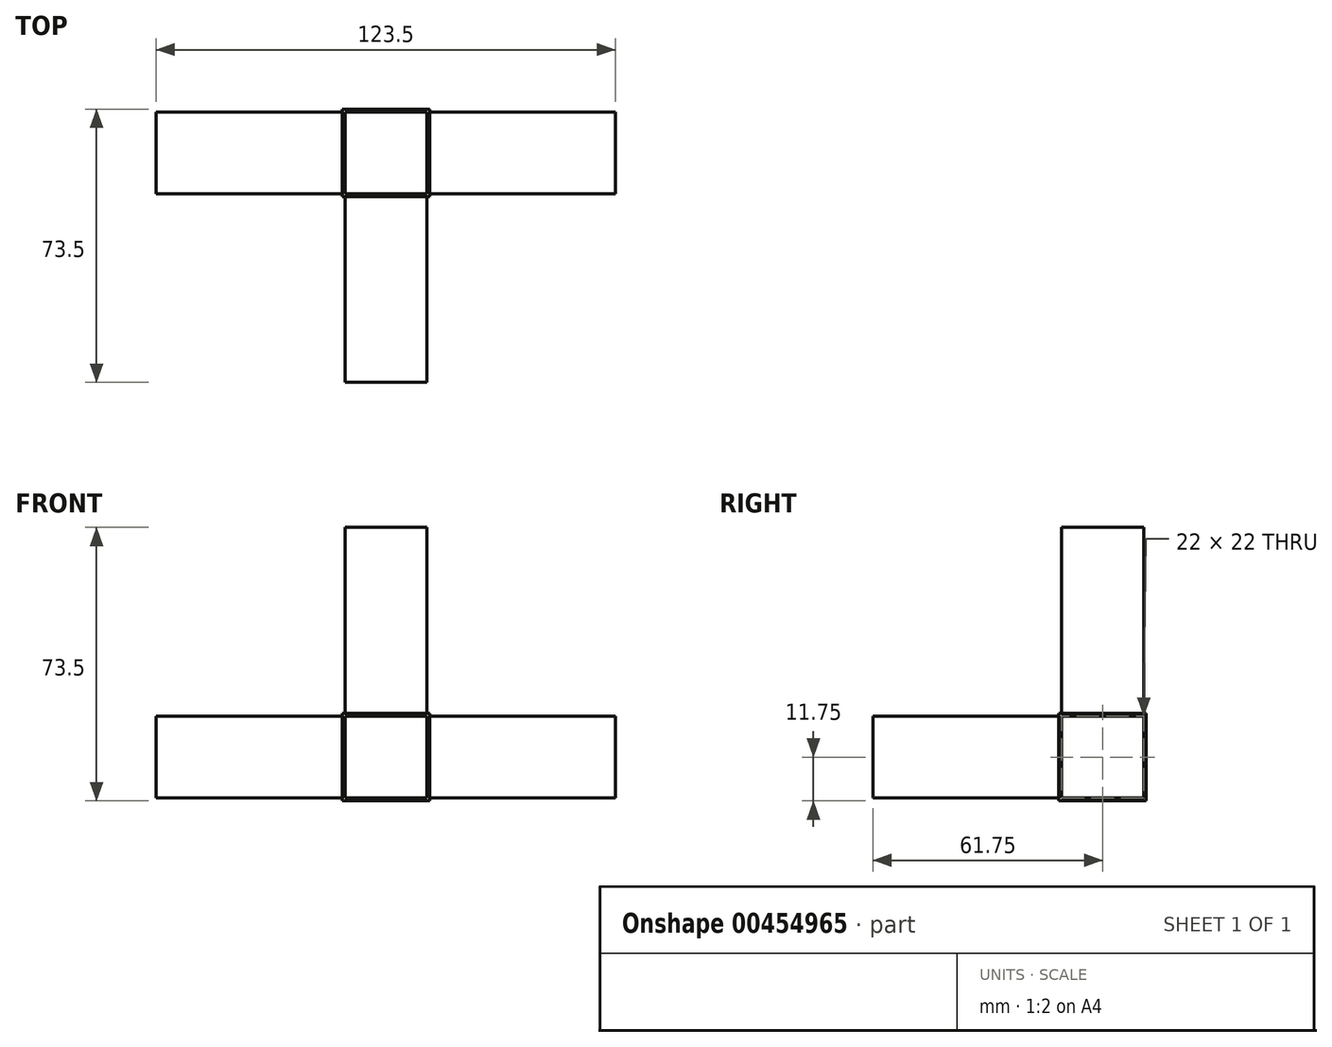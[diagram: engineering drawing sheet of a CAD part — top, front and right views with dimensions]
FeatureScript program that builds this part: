
annotation { "Feature Type Name" : "Feature", "Feature Type Description" : "" }
export const myFeature = defineFeature(function(context is Context, id is Id, definition is map)
    precondition{}
    {
        {
            var Q0;
            Q0=qCreatedBy(makeId("Front.planeOp"),FACE);
            var sketch = newSketch(context, id + "F0", { "sketchPlane" : qUnion([Q0])});
            skLineSegment(sketch, "E0.bottom", {"start": v(11.75, 11.75) * mm, "end": v(-11.75, 11.75) * mm});
            skLineSegment(sketch, "E0.top", {"start": v(11.75, -11.75) * mm, "end": v(-11.75, -11.75) * mm});
            skLineSegment(sketch, "E0.left", {"start": v(11.75, 11.75) * mm, "end": v(11.75, -11.75) * mm});
            skLineSegment(sketch, "E0.right", {"start": v(-11.75, 11.75) * mm, "end": v(-11.75, -11.75) * mm});
            skPoint(sketch, "E0.middle", {"position": v(0, 0) * mm});
            skSolve(sketch);
        }
        {
            var Q0;
            Q0 = qSketchRegion(id + "F0", true);
            extrude(context, id + "F1", {"entities" : qUnion([Q0]), "endBound" : BoundingType.SYMMETRIC, "depth" : 23.5 * mm});
        }
        {
            var Q0;
            Q0=makeQuery(id+"F1.opExtrude","CAP_FACE",FACE,{"disambiguationData":[OSD([sQuery(id+"F0.wireOp",EDGE,"E0.bottom"),sQuery(id+"F0.wireOp",EDGE,"E0.top"),sQuery(id+"F0.wireOp",EDGE,"E0.left"),sQuery(id+"F0.wireOp",EDGE,"E0.right")])],"isStart":false});
            var sketch = newSketch(context, id + "F2", { "sketchPlane" : qUnion([Q0])});
            skLineSegment(sketch, "E1.bottom", {"start": v(11, 11) * mm, "end": v(-11, 11) * mm});
            skLineSegment(sketch, "E1.top", {"start": v(11, -11) * mm, "end": v(-11, -11) * mm});
            skLineSegment(sketch, "E1.left", {"start": v(11, 11) * mm, "end": v(11, -11) * mm});
            skLineSegment(sketch, "E1.right", {"start": v(-11, 11) * mm, "end": v(-11, -11) * mm});
            skPoint(sketch, "E1.middle", {"position": v(0, 0) * mm});
            skSolve(sketch);
        }
        {
            var Q0;
            Q0 = qSketchRegion(id + "F2", true);
            extrude(context, id + "F3", {"entities" : qUnion([Q0]), "operationType" : NewBodyOperationType.ADD, "depth" : 50 * mm});
        }
        {
            var Q0;
            Q0=makeQuery(id+"F1.opExtrude","SWEPT_FACE",FACE,{"disambiguationData":[OSD([sQuery(id+"F0.wireOp",EDGE,"E0.left")])]});
            var sketch = newSketch(context, id + "F4", { "sketchPlane" : qUnion([Q0])});
            skLineSegment(sketch, "E2.bottom", {"start": v(11, 11) * mm, "end": v(-11, 11) * mm});
            skLineSegment(sketch, "E2.top", {"start": v(11, -11) * mm, "end": v(-11, -11) * mm});
            skLineSegment(sketch, "E2.left", {"start": v(11, 11) * mm, "end": v(11, -11) * mm});
            skLineSegment(sketch, "E2.right", {"start": v(-11, 11) * mm, "end": v(-11, -11) * mm});
            skPoint(sketch, "E2.middle", {"position": v(0, 0) * mm});
            skSolve(sketch);
        }
        {
            var Q0;
            Q0 = qSketchRegion(id + "F4", true);
            extrude(context, id + "F5", {"entities" : qUnion([Q0]), "operationType" : NewBodyOperationType.ADD, "depth" : 50 * mm});
        }
        {
            var Q0;
            Q0=makeQuery(id+"F1.opExtrude","SWEPT_FACE",FACE,{"disambiguationData":[OSD([sQuery(id+"F0.wireOp",EDGE,"E0.right")])]});
            var sketch = newSketch(context, id + "F6", { "sketchPlane" : qUnion([Q0])});
            skLineSegment(sketch, "E3.bottom", {"start": v(11, 11) * mm, "end": v(-11, 11) * mm});
            skLineSegment(sketch, "E3.top", {"start": v(11, -11) * mm, "end": v(-11, -11) * mm});
            skLineSegment(sketch, "E3.left", {"start": v(11, 11) * mm, "end": v(11, -11) * mm});
            skLineSegment(sketch, "E3.right", {"start": v(-11, 11) * mm, "end": v(-11, -11) * mm});
            skPoint(sketch, "E3.middle", {"position": v(0, 0) * mm});
            skSolve(sketch);
        }
        {
            var Q0;
            Q0 = qSketchRegion(id + "F6", true);
            extrude(context, id + "F7", {"entities" : qUnion([Q0]), "operationType" : NewBodyOperationType.ADD, "depth" : 50 * mm});
        }
        {
            var Q0;
            Q0=makeQuery(id+"F1.opExtrude","SWEPT_FACE",FACE,{"disambiguationData":[OSD([sQuery(id+"F0.wireOp",EDGE,"E0.bottom")])]});
            var sketch = newSketch(context, id + "F8", { "sketchPlane" : qUnion([Q0])});
            skLineSegment(sketch, "E4.bottom", {"start": v(11, 11) * mm, "end": v(-11, 11) * mm});
            skLineSegment(sketch, "E4.top", {"start": v(11, -11) * mm, "end": v(-11, -11) * mm});
            skLineSegment(sketch, "E4.left", {"start": v(11, 11) * mm, "end": v(11, -11) * mm});
            skLineSegment(sketch, "E4.right", {"start": v(-11, 11) * mm, "end": v(-11, -11) * mm});
            skPoint(sketch, "E4.middle", {"position": v(0, 0) * mm});
            skSolve(sketch);
        }
        {
            var Q0;
            Q0 = qSketchRegion(id + "F8", true);
            extrude(context, id + "F9", {"entities" : qUnion([Q0]), "operationType" : NewBodyOperationType.ADD, "depth" : 50 * mm});
        }
    });
